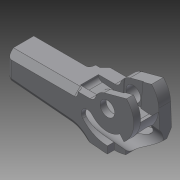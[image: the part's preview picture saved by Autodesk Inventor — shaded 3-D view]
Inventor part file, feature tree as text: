
AUTODESK INVENTOR PART (.ipt)
format: ipt  version: 2014 SP1 (Build 180222100, 222)  size: 1,937,920 bytes
history: native  units: in
note: dims shown in document units (in); Inventor stores cm internally (conversion verified against a paired STEP export)
features: sketch x19, projected_geometry x19, extrude x9, revolve x5, fillet x3, sweep x3, other x2, plane x1, mirror x1, chamfer x1
ambient origin geometry x8: Origin, YZ Plane, XZ Plane, XY Plane, X Axis, Y Axis, Z Axis, Center Point
bodies: Solid1 (feature_tree)
feature tree (63):
  other  "Hammer"
  extrude  "Extrusion1"  Depth=1.4117in
  revolve  "Revolution1"  [1 undecoded]
  extrude  "Extrusion2"  Depth=0.0575in
  revolve  "Revolution2"  [1 undecoded]
  extrude  "Extrusion4"  TaperAngle=15.0deg  [1 undecoded]
  extrude  "Extrusion6"  Depth=0.0775in
  fillet  "Fillet1"  Radius=0.81in
  extrude  "Extrusion7"  Depth=0.351in TaperAngle=0.0deg
  extrude  "Extrusion8"  TaperAngle=45.0deg  [1 undecoded]
  extrude  "Extrusion9"  Depth=0.0075in
  extrude  "Extrusion10"  Depth=1.0in TaperAngle=0.0deg
  extrude  "Extrusion11"  Depth=1.324in
  revolve  "Revolution3"  [1 undecoded]
  sketch  "Sketch17"  dims[d104=0.2in d105=0.0in d106=0.157in d107=0.002in]
  sketch  "Sketch16"  dims[d98=0.0975in d99=0.0in d103=0.72in]
  sweep  "Sweep1"
  sweep  "Sweep2"
  fillet  "Fillet2"  Radius=0.002in
  sketch  "Sketch18"  dims[d108=0.2in d109=0.0in d110=0.1985in]
  plane  "Work Plane1"
  sweep  "Sweep3"
  revolve  "Revolution4"  [1 undecoded]
  mirror  "Mirror1"
  chamfer  "Chamfer1"  [1 undecoded]
  fillet  "Fillet3"  Radius=0.2175in
  revolve  "Revolution5"  Angle=180.0deg
  sketch  "Sketch1"  dims[d1=0.161in d4=1.4117in]
  other  "Image1"
  sketch  "Sketch2"  dims[d9=0.1385in d10=0.2085in]
  sketch  "Sketch3"  dims[d12=0.135in d17=0.0575in]
  projected_geometry  "Projected Loop1"
  projected_geometry  "Projected Loop2"
  projected_geometry  "Projected Loop3"
  sketch  "Sketch4"  dims[d18=0.0625in d36=0.1385in]
  sketch  "Sketch6"  dims[d37=0.135in d38=15.0deg]
  projected_geometry  "Projected Loop5"
  sketch  "Sketch9"  dims[d40=0.117in d48=0.0775in d54=0.81in]
  sketch  "Sketch10"  dims[d55=0.6528in d81=0.351in d82=0.0in]
  projected_geometry  "Projected Loop8"
  projected_geometry  "Projected Loop9"
  sketch  "Sketch11"  dims[d83=0.055in d84=45.0deg]
  projected_geometry  "Projected Loop10"
  sketch  "Sketch12"  dims[d85=0.271in d86=0.0075in]
  projected_geometry  "Projected Loop11"
  sketch  "Sketch13"  dims[d87=90.0deg d88=1.0in d89=0.0in]
  sketch  "Sketch14"  dims[d90=0.273in d91=1.324in]
  sketch  "Sketch15"  dims[d92=90.0deg d97=0.109in]
  projected_geometry  "Projected Loop12"
  projected_geometry  "Projected Loop13"
  sketch  "Sketch19"  dims[d111=0.2175in d112=0.0in d114=0.2175in d115=0.0in d116=0.0in d117=0.0in d118=0.2175in d119=0.0in]
  projected_geometry  "Projected Loop14"
  sketch  "Sketch20"  dims[d120=0.0225in d121=180.0deg]
  sketch  "Sketch21"  dims[d122=45.0deg]
  projected_geometry  "Projected Loop15"
  sketch  "Sketch22"  dims[d123=45.0deg d124=0.0895in d125=0.0in d126=0.0in d127=0.0447in d128=0.0398in d129=90.0deg d130=0.0in d131=90.0deg d132=0.015in d133=0.125in d134=45.0deg d135=0.04in d136=0.0195in d137=180.0deg]
  projected_geometry  "Project Cut Edges1"
  projected_geometry  "Project Cut Edges2"
  projected_geometry  "Project Cut Edges3"
  projected_geometry  "Project Cut Edges4"
  projected_geometry  "Project Cut Edges5"
  projected_geometry  "Project Cut Edges6"
  projected_geometry  "Project Cut Edges7"
note: 7 required parameter values undecoded (feature->parameter linkage not recoverable at this tier; creation-order binding heuristic only, values carry confidence <= 0.55)